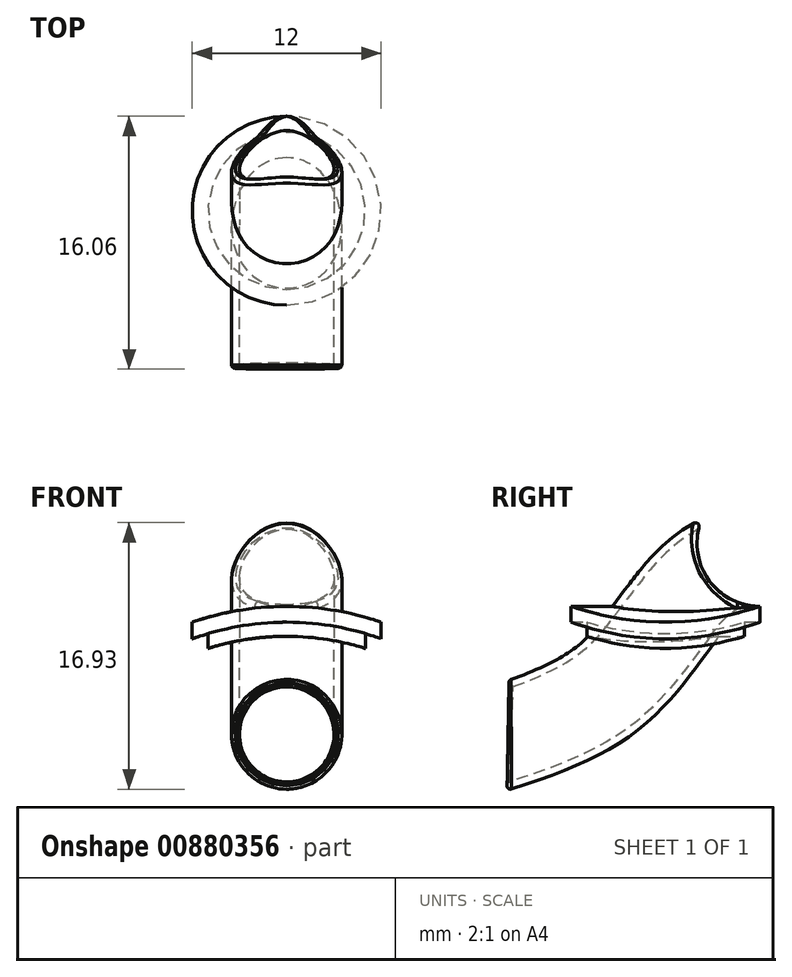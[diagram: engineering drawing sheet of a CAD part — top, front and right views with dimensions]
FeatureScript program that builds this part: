
annotation { "Feature Type Name" : "Feature", "Feature Type Description" : "" }
export const myFeature = defineFeature(function(context is Context, id is Id, definition is map)
    precondition{}
    {
        {
            var Q0;
            Q0=qCreatedBy(makeId("Front.planeOp"),FACE);
            var sketch = newSketch(context, id + "F0", { "sketchPlane" : qUnion([Q0])});
            skCircle(sketch, "E0", {"center": v(0, 0) * mm, "radius": 17.5 * mm});
            skCircle(sketch, "E1.0", {"center": v(0, 0) * mm, "radius": 16.6 * mm});
            skSolve(sketch);
        }
        {
            var Q0;
            Q0=makeQuery(id+"F0.imprint","IMPRINT",FACE,{"disambiguationData":[TD([[makeQuery(id+"F0.imprint","IMPRINT",EDGE,{"derivedFrom":sQuery(id+"F0.wireOp",EDGE,"E0")}),1.0]])]});
            extrude(context, id + "F1", {"entities" : qUnion([Q0]), "endBound" : BoundingType.SYMMETRIC, "depth" : 25 * mm, "offsetDistance" : 25 * mm});
        }
        {
            var Q0;
            Q0=qCreatedBy(makeId("Top.planeOp"),FACE);
            var sketch = newSketch(context, id + "F2", { "sketchPlane" : qUnion([Q0])});
            skCircle(sketch, "E2", {"center": v(0, 0) * mm, "radius": 5 * mm});
            skSolve(sketch);
        }
        {
            var Q0;
            Q0 = qSketchRegion(id + "F2", true);
            extrude(context, id + "F3", {"entities" : qUnion([Q0]), "operationType" : NewBodyOperationType.INTERSECT, "depth" : 25 * mm, "offsetDistance" : 25 * mm});
        }
        {
            var Q0;
            Q0=qCreatedBy(makeId("Front.planeOp"),FACE);
            var sketch = newSketch(context, id + "F4", { "sketchPlane" : qUnion([Q0])});
            skCircle(sketch, "E3", {"center": v(0, 0) * mm, "radius": 18.5 * mm});
            skCircle(sketch, "E4.0", {"center": v(0, 0) * mm, "radius": 17.5 * mm});
            skSolve(sketch);
        }
        {
            var Q0;
            Q0=makeQuery(id+"F4.imprint","IMPRINT",FACE,{"disambiguationData":[TD([[makeQuery(id+"F4.imprint","IMPRINT",EDGE,{"derivedFrom":sQuery(id+"F4.wireOp",EDGE,"E3")}),1.0]])]});
            extrude(context, id + "F5", {"entities" : qUnion([Q0]), "operationType" : NewBodyOperationType.ADD, "endBound" : BoundingType.SYMMETRIC, "depth" : 25 * mm, "offsetDistance" : 25 * mm});
        }
        {
            var Q0;
            Q0=qCreatedBy(makeId("Top.planeOp"),FACE);
            var sketch = newSketch(context, id + "F6", { "sketchPlane" : qUnion([Q0])});
            skCircle(sketch, "E5", {"center": v(0, 0) * mm, "radius": 6 * mm});
            skSolve(sketch);
        }
        {
            var Q0;
            Q0=makeQuery(id+"F6.imprint","IMPRINT",FACE,{"disambiguationData":[TD([[makeQuery(id+"F6.imprint","IMPRINT",EDGE,{"derivedFrom":sQuery(id+"F6.wireOp",EDGE,"E5")}),1.0]])]});
            extrude(context, id + "F7", {"entities" : qUnion([Q0]), "operationType" : NewBodyOperationType.INTERSECT, "depth" : 25 * mm, "offsetDistance" : 25 * mm});
        }
        {
            var Q0;
            Q0=qCreatedBy(makeId("Right.planeOp"),FACE);
            var sketch = newSketch(context, id + "F8", { "sketchPlane" : qUnion([Q0])});
            skFitSpline(sketch, "E6", {"points": [v(-10, 10.31) * mm, v(-2.58, 14.38) * mm, v(1.4, 19.22) * mm, v(6, 22) * mm], "startDerivative": vector(29.78, 9.95) * mm, "endDerivative": vector(23.36, 8.28) * mm});
            skSolve(sketch);
        }
        {
            var Q0;
            Q0=qCreatedBy(makeId("Front.planeOp"),FACE);
            cPlane(context, id + "F9", {"entities" : qUnion([Q0]), "cplaneType" : CPlaneType.OFFSET, "offset" : 6 * mm, "oppositeDirection" : true, "width" : 150 * mm, "height" : 150 * mm});
        }
        {
            var Q0;
            Q0=qCreatedBy(id+"F9.planeOp",FACE);
            var sketch = newSketch(context, id + "F10", { "sketchPlane" : qUnion([Q0])});
            skCircle(sketch, "E7", {"center": v(0, 22) * mm, "radius": 3.5 * mm});
            skCircle(sketch, "E8.0", {"center": v(0, 22) * mm, "radius": 3 * mm});
            skSolve(sketch);
        }
        {
            var Q0;
            Q0=makeQuery(id+"F10.imprint","IMPRINT",FACE,{"disambiguationData":[TD([[makeQuery(id+"F10.imprint","IMPRINT",EDGE,{"derivedFrom":sQuery(id+"F10.wireOp",EDGE,"E7")}),1.0]])]});
            var Q1;
            Q1 = qConstructionFilter(qBodyType(qCreatedBy(id + "F8" ,EDGE), BodyType.WIRE), ConstructionObject.NO);
            sweep(context, id + "F11", {"operationType" : NewBodyOperationType.ADD, "profiles" : qUnion([Q0]), "path" : qUnion([Q1])});
        }
        {
            var Q0;
            Q0=makeQuery(id+"F10.imprint","IMPRINT",FACE,{"disambiguationData":[TD([[makeQuery(id+"F10.imprint","IMPRINT",EDGE,{"derivedFrom":sQuery(id+"F10.wireOp",EDGE,"E8.0")}),1.0]])]});
            var Q1;
            Q1 = qConstructionFilter(qBodyType(qCreatedBy(id + "F8" ,EDGE), BodyType.WIRE), ConstructionObject.NO);
            sweep(context, id + "F12", {"operationType" : NewBodyOperationType.REMOVE, "profiles" : qUnion([Q0]), "path" : qUnion([Q1])});
        }
        {
            var Q0;
            Q0=qCreatedBy(makeId("Right.planeOp"),FACE);
            var sketch = newSketch(context, id + "F13", { "sketchPlane" : qUnion([Q0])});
            skCircle(sketch, "E9", {"center": v(6, 22.5) * mm, "radius": 4 * mm});
            skSolve(sketch);
        }
        {
            var Q0;
            Q0=makeQuery(id+"F13.imprint","IMPRINT",FACE,{"disambiguationData":[TD([[makeQuery(id+"F13.imprint","IMPRINT",EDGE,{"derivedFrom":sQuery(id+"F13.wireOp",EDGE,"E9")}),1.0]])]});
            extrude(context, id + "F14", {"entities" : qUnion([Q0]), "operationType" : NewBodyOperationType.REMOVE, "endBound" : BoundingType.SYMMETRIC, "oppositeDirection" : true, "depth" : 25 * mm, "offsetDistance" : 25 * mm});
        }
        {
            var Q0;
            {var subQ0=sQuery(id+"F10.wireOp",EDGE,"E7");Q0=makeQuery(id+"F14.boolean.opBoolean","INTERSECT",EDGE,{"derivedFrom":[makeQuery(id+"F11.boolean.opBoolean","SPLIT",FACE,{"disambiguationData":[TD([makeQuery(id+"F5.opExtrude","SWEPT_FACE",FACE,{"disambiguationData":[OSD([sQuery(id+"F4.wireOp",EDGE,"E3")])]})])],"derivedFrom":makeQuery(id+"F11.opSweep","SWEPT_FACE",FACE,{"disambiguationData":[OSD([sQuery(id+"F8.wireOp",EDGE,"E6"),subQ0])]})}),makeQuery(id+"F14.opExtrude","SWEPT_FACE",FACE,{"disambiguationData":[OSD([sQuery(id+"F13.wireOp",EDGE,"E9")])]})]});}
            fillet(context, id + "F15", {"entities" : qUnion([Q0]), "radius" : 0.25 * mm, "tangentPropagation" : true, "allowEdgeOverflow" : false});
        }
        {
            var Q0;
            Q0=makeQuery(id+"F11.opSweep","CAP_EDGE",EDGE,{"disambiguationData":[OSD([sQuery(id+"F8.wireOp",VERTEX,"E6.start"),sQuery(id+"F10.wireOp",EDGE,"E7")])],"isStart":false});
            var Q1;
            Q1=makeQuery(id+"F11.opSweep","CAP_EDGE",EDGE,{"disambiguationData":[OSD([sQuery(id+"F8.wireOp",VERTEX,"E6.start"),sQuery(id+"F10.wireOp",EDGE,"E8.0")])],"isStart":false});
            fillet(context, id + "F16", {"entities" : qUnion([Q0, Q1]), "radius" : 0.2 * mm, "tangentPropagation" : true, "allowEdgeOverflow" : false});
        }
    });
